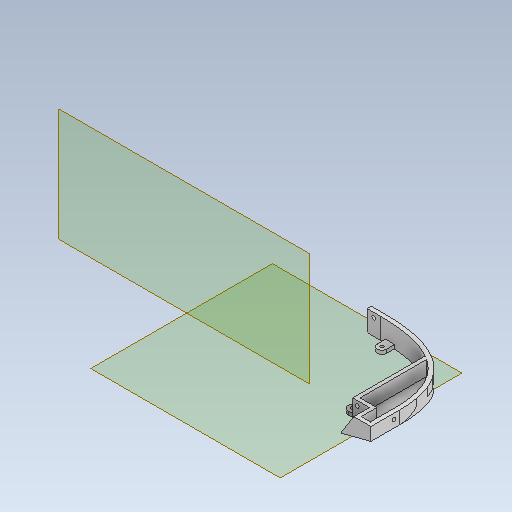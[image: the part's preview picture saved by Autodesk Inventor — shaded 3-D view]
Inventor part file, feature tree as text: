
AUTODESK INVENTOR PART (.ipt)
format: ipt  version: 2020 (Build 240168000, 168)  size: 250,880 bytes
history: native  units: mm
features: sketch x14, other x6
ambient origin geometry x8: Origin, YZ Plane, XZ Plane, XY Plane, X Axis, Y Axis, Z Axis, Center Point
bodies: Body1 (feature_tree)
feature tree (20):
  other  "canto.ipt"
  other  "Sólido2::canto.ipt"
  other  "OperaçãoIdentificador1"
  sketch  "Esboço7"  dims[d0=10.0mm]
  sketch  "Esboço8"
  sketch  "Esboço9"
  sketch  "Esboço10"
  sketch  "Esboço11"
  sketch  "Esboço12"
  sketch  "Esboço13"
  sketch  "Esboço14"
  sketch  "Esboço15"
  sketch  "Esboço16"
  sketch  "Esboço17"
  sketch  "Esboço18"
  sketch  "Esboço20"
  sketch  "Esboço21"
  other  "Plano de trabalho1"
  other  "Plano de trabalho2"
  other  "Sólido1"
